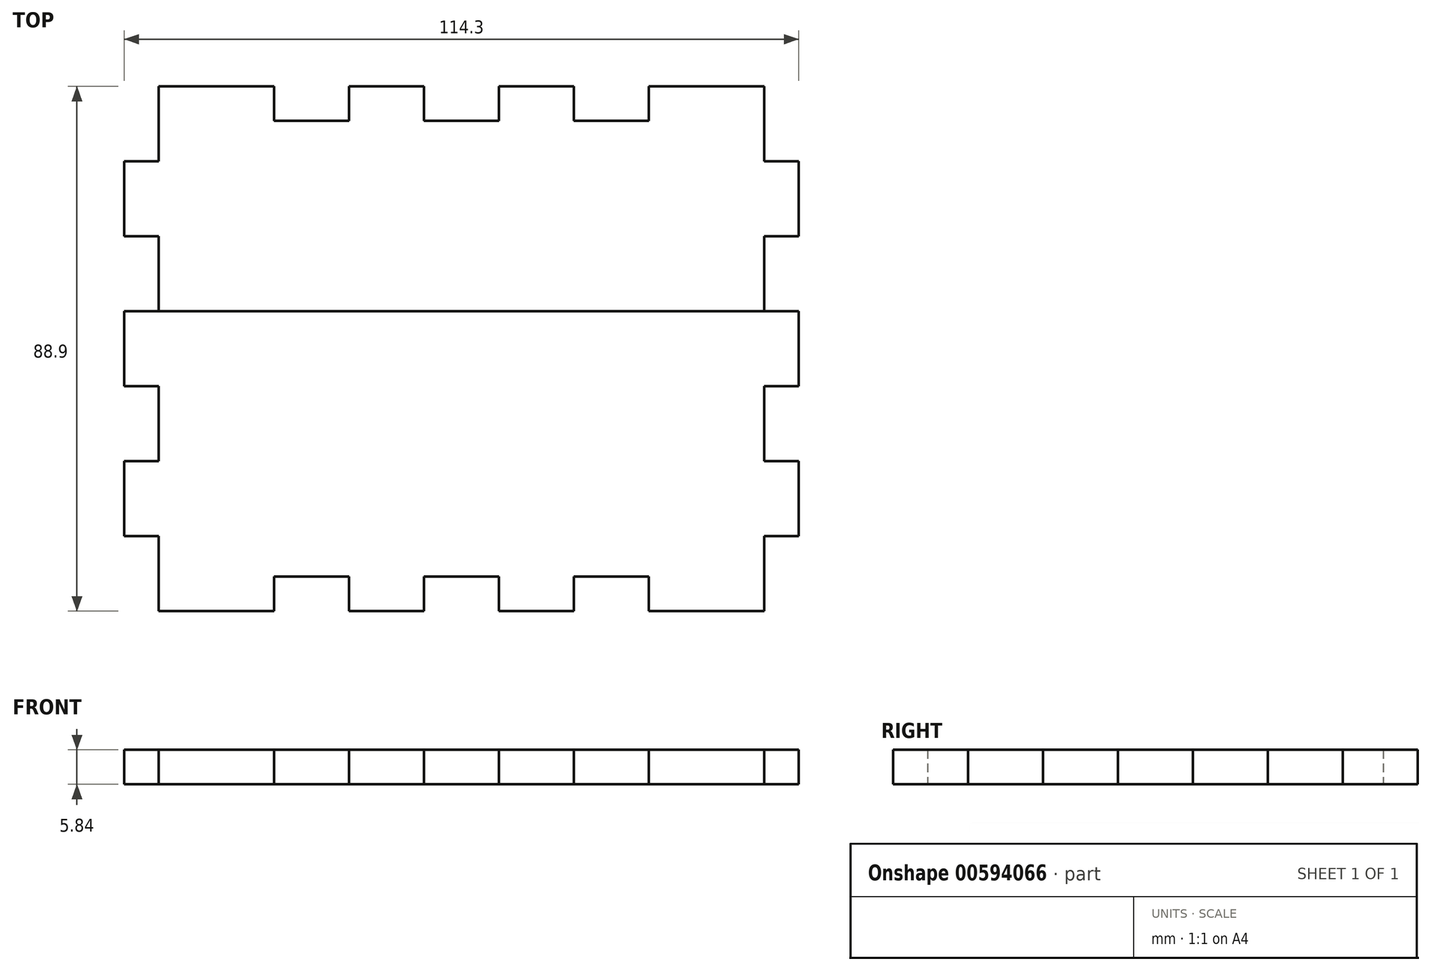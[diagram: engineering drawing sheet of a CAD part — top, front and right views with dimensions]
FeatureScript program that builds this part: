
annotation { "Feature Type Name" : "Feature", "Feature Type Description" : "" }
export const myFeature = defineFeature(function(context is Context, id is Id, definition is map)
    precondition{}
    {
        {
            var Q0;
            Q0=qCreatedBy(makeId("Top.planeOp"),FACE);
            var sketch = newSketch(context, id + "F0", { "sketchPlane" : qUnion([Q0])});
            skLineSegment(sketch, "E0.bottom", {"start": v(5.84, 0) * mm, "end": v(25.4, 0) * mm});
            skLineSegment(sketch, "E0.left", {"start": v(0, -12.7) * mm, "end": v(0, -25.4) * mm});
            skLineSegment(sketch, "E1", {"start": v(5.84, 0) * mm, "end": v(5.84, -12.7) * mm});
            skLineSegment(sketch, "E2", {"start": v(5.84, -12.7) * mm, "end": v(0, -12.7) * mm});
            skPoint(sketch, "E3.orphan", {"position": v(0, 0) * mm});
            skLineSegment(sketch, "E4", {"start": v(25.4, 0) * mm, "end": v(25.4, -5.84) * mm});
            skLineSegment(sketch, "E5", {"start": v(25.4, -5.84) * mm, "end": v(38.1, -5.84) * mm});
            skLineSegment(sketch, "E6", {"start": v(38.1, -5.84) * mm, "end": v(38.1, 0) * mm});
            skLineSegment(sketch, "E7", {"start": v(38.1, 0) * mm, "end": v(50.8, 0) * mm});
            skLineSegment(sketch, "E8", {"start": v(50.8, 0) * mm, "end": v(50.8, -5.84) * mm});
            skLineSegment(sketch, "E9", {"start": v(50.8, -5.84) * mm, "end": v(63.5, -5.84) * mm});
            skLineSegment(sketch, "E10", {"start": v(63.5, -5.84) * mm, "end": v(63.5, 0) * mm});
            skLineSegment(sketch, "E11", {"start": v(63.5, 0) * mm, "end": v(76.2, 0) * mm});
            skLineSegment(sketch, "E12", {"start": v(76.2, 0) * mm, "end": v(76.2, -5.84) * mm});
            skLineSegment(sketch, "E13", {"start": v(76.2, -5.84) * mm, "end": v(88.9, -5.84) * mm});
            skLineSegment(sketch, "E14", {"start": v(88.9, -5.84) * mm, "end": v(88.9, 0) * mm});
            skLineSegment(sketch, "E15.trimOffspring", {"start": v(88.9, 0) * mm, "end": v(108.46, 0) * mm});
            skLineSegment(sketch, "E16", {"start": v(108.46, 0) * mm, "end": v(108.46, -12.7) * mm});
            skLineSegment(sketch, "E17", {"start": v(108.46, -12.7) * mm, "end": v(114.3, -12.7) * mm});
            skPoint(sketch, "E18.orphan", {"position": v(114.3, 0) * mm});
            skLineSegment(sketch, "E19", {"start": v(0, -25.4) * mm, "end": v(5.84, -25.4) * mm});
            skLineSegment(sketch, "E20", {"start": v(5.84, -25.4) * mm, "end": v(5.84, -38.1) * mm});
            skLineSegment(sketch, "E21", {"start": v(5.84, -38.1) * mm, "end": v(0, -38.1) * mm});
            skLineSegment(sketch, "E22", {"start": v(0, -38.1) * mm, "end": v(0, -50.8) * mm});
            skLineSegment(sketch, "E23", {"start": v(0, -50.8) * mm, "end": v(5.84, -50.8) * mm});
            skLineSegment(sketch, "E24", {"start": v(5.84, -50.8) * mm, "end": v(5.84, -63.5) * mm});
            skLineSegment(sketch, "E25", {"start": v(5.84, -63.5) * mm, "end": v(0, -63.5) * mm});
            skLineSegment(sketch, "E26.trimOffspring", {"start": v(0, -63.5) * mm, "end": v(0, -76.2) * mm});
            skLineSegment(sketch, "E27", {"start": v(0, -76.2) * mm, "end": v(5.84, -76.2) * mm});
            skLineSegment(sketch, "E28", {"start": v(5.84, -76.2) * mm, "end": v(5.84, -88.9) * mm});
            skPoint(sketch, "E29.orphan", {"position": v(0, -88.9) * mm});
            skLineSegment(sketch, "E30", {"start": v(57.15, -5.84) * mm, "end": v(57.15, -25.82) * mm, "construction": true});
            skLineSegment(sketch, "E31", {"start": v(0, -44.45) * mm, "end": v(13.93, -44.45) * mm, "construction": true});
            skLineSegment(sketch, "E32.MirrorCS", {"start": v(114.3, -12.7) * mm, "end": v(114.3, -25.4) * mm});
            skLineSegment(sketch, "E33.MirrorCS", {"start": v(114.3, -25.4) * mm, "end": v(108.46, -25.4) * mm});
            skLineSegment(sketch, "E34.MirrorCS", {"start": v(108.46, -25.4) * mm, "end": v(108.46, -38.1) * mm});
            skLineSegment(sketch, "E35.MirrorCS", {"start": v(108.46, -38.1) * mm, "end": v(114.3, -38.1) * mm});
            skLineSegment(sketch, "E36.MirrorCS", {"start": v(114.3, -38.1) * mm, "end": v(114.3, -50.8) * mm});
            skLineSegment(sketch, "E37.MirrorCS", {"start": v(114.3, -50.8) * mm, "end": v(108.46, -50.8) * mm});
            skLineSegment(sketch, "E38.MirrorCS", {"start": v(108.46, -50.8) * mm, "end": v(108.46, -63.5) * mm});
            skLineSegment(sketch, "E39.MirrorCS", {"start": v(108.46, -63.5) * mm, "end": v(114.3, -63.5) * mm});
            skLineSegment(sketch, "E40.MirrorCS", {"start": v(114.3, -63.5) * mm, "end": v(114.3, -76.2) * mm});
            skLineSegment(sketch, "E41.MirrorCS", {"start": v(114.3, -76.2) * mm, "end": v(108.46, -76.2) * mm});
            skLineSegment(sketch, "E42.MirrorCS", {"start": v(108.46, -76.2) * mm, "end": v(108.46, -88.9) * mm});
            skLineSegment(sketch, "E43.MirrorCS", {"start": v(5.84, -88.9) * mm, "end": v(25.4, -88.9) * mm});
            skLineSegment(sketch, "E44.MirrorCS", {"start": v(25.4, -88.9) * mm, "end": v(25.4, -83.06) * mm});
            skLineSegment(sketch, "E45.MirrorCS", {"start": v(25.4, -83.06) * mm, "end": v(38.1, -83.06) * mm});
            skLineSegment(sketch, "E46.MirrorCS", {"start": v(38.1, -83.06) * mm, "end": v(38.1, -88.9) * mm});
            skLineSegment(sketch, "E47.MirrorCS", {"start": v(38.1, -88.9) * mm, "end": v(50.8, -88.9) * mm});
            skLineSegment(sketch, "E48.MirrorCS", {"start": v(50.8, -88.9) * mm, "end": v(50.8, -83.06) * mm});
            skLineSegment(sketch, "E49.MirrorCS", {"start": v(50.8, -83.06) * mm, "end": v(63.5, -83.06) * mm});
            skLineSegment(sketch, "E50.MirrorCS", {"start": v(63.5, -83.06) * mm, "end": v(63.5, -88.9) * mm});
            skLineSegment(sketch, "E51.MirrorCS", {"start": v(63.5, -88.9) * mm, "end": v(76.2, -88.9) * mm});
            skLineSegment(sketch, "E52.MirrorCS", {"start": v(76.2, -88.9) * mm, "end": v(76.2, -83.06) * mm});
            skLineSegment(sketch, "E53.MirrorCS", {"start": v(76.2, -83.06) * mm, "end": v(88.9, -83.06) * mm});
            skLineSegment(sketch, "E54.MirrorCS", {"start": v(88.9, -83.06) * mm, "end": v(88.9, -88.9) * mm});
            skLineSegment(sketch, "E55.MirrorCS", {"start": v(88.9, -88.9) * mm, "end": v(108.46, -88.9) * mm});
            skLineSegment(sketch, "E56", {"start": v(5.84, -38.1) * mm, "end": v(108.46, -38.1) * mm});
            skSolve(sketch);
        }
        {
            var Q0;
            Q0=makeQuery(id+"F0.imprint","IMPRINT",FACE,{"disambiguationData":[TD([[makeQuery(id+"F0.imprint","IMPRINT",EDGE,{"derivedFrom":sQuery(id+"F0.wireOp",EDGE,"E1")}),1.0]])]});
            extrude(context, id + "F1", {"entities" : qUnion([Q0]), "depth" : 5.84 * mm, "offsetDistance" : 25.4 * mm});
        }
        {
            var Q0;
            Q0=makeQuery(id+"F0.imprint","IMPRINT",FACE,{"disambiguationData":[TD([[makeQuery(id+"F0.imprint","IMPRINT",EDGE,{"derivedFrom":sQuery(id+"F0.wireOp",EDGE,"E21")}),1.0]])]});
            extrude(context, id + "F2", {"entities" : qUnion([Q0]), "depth" : 5.84 * mm, "offsetDistance" : 25.4 * mm});
        }
    });
